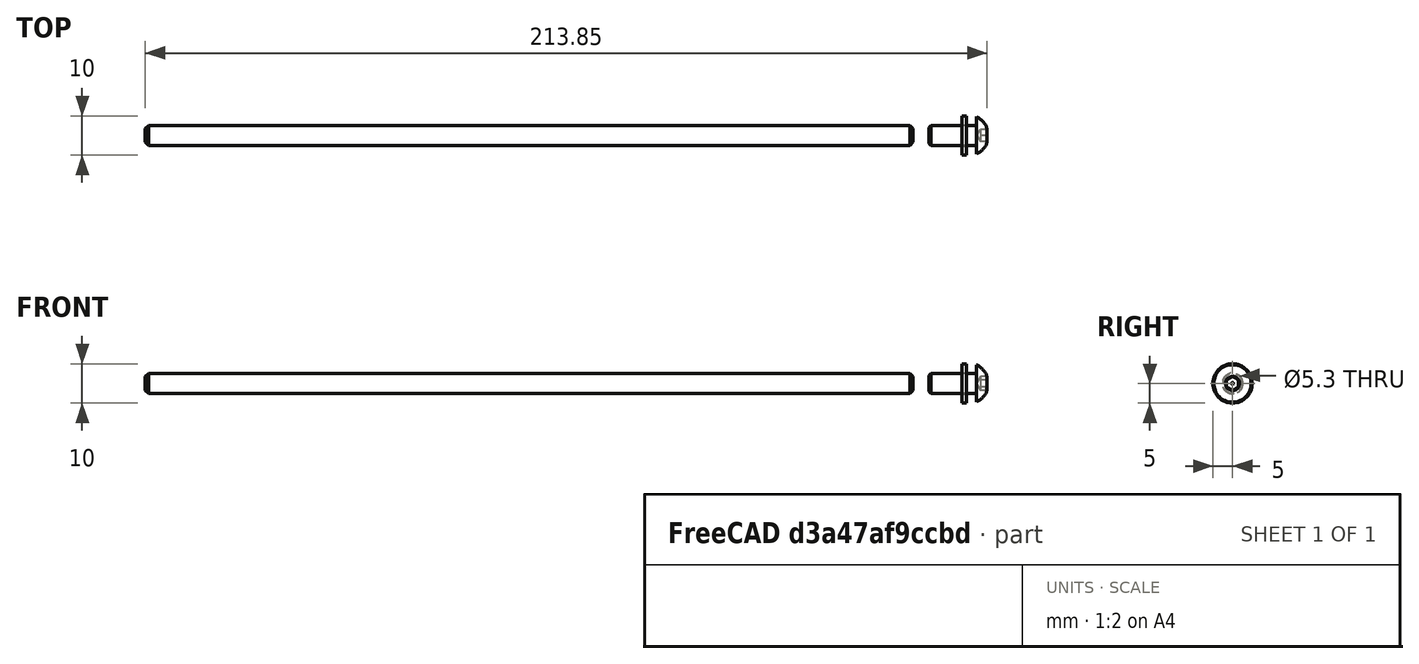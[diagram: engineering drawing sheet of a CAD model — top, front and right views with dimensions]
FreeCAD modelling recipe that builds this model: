
FCSTD DOCUMENT  (FreeCAD 0.21R38887 (Git))
Label: РоликY
License: All rights reserved
LicenseURL: http://en.wikipedia.org/wiki/All_rights_reserved
objects: App::FeaturePython×31, Part::FeaturePython×22, App::Link×7
note: 21 computed .brp shape members not serialized (recipe doc carries the construction recipe); baked Part::Feature solids carry a one-line shape summary decoded from their .brp
EXTERNAL_REF file=ТаблицаПараметров.FCStd obj=Spreadsheet002
EXTERNAL_REF file=роликЗащитыY.FCStd obj=Body
EXTERNAL_REF file=подшипник.FCStd obj=Body
EXTERNAL_REF file=Крепеж.FCStd obj=Body003
EXTERNAL_REF file=ТаблицаПараметров.FCStd obj=Spreadsheet004

FEATURE [Part::FeaturePython] Washer  label="M5-Washer"  # Fasteners workbench fastener (typed FeaturePython)
  InvalidShape = false
  Placement = pos=(110.2,-4e-16,2.59e-14) rot=(-0.707107,0,-0.707107;3.14159rad)
  TreeRank = 2
  ValidateShape = false
  diameter = 6
  invert = false
  matchOuter = false
  offset = 0
  type = 3
  expr: diameter = <<ТаблицаПараметров>>#<<Ролик>>.ShaibaIndex
FEATURE [App::Link] Link003  label="ШайбаПрав"
  AutoLinkLabel = true
  AutoPlacement = true
  LinkPlacement = pos=(-109.5,1e-15,2.55e-14) rot=(0,-1,0;4.71239rad)
  LinkedObject = -> Washer
  Placement = pos=(-109.5,1e-15,2.55e-14) rot=(0,-1,0;4.71239rad)
  SyncGroupVisibility = false
  TreeRank = 4
  _LinkVersion = 1
FEATURE [App::Link] Link006  label="РоликТело"
  AutoLinkLabel = false
  AutoPlacement = true
  LinkPlacement = pos=(1,-4e-16,2.51e-14) rot=(0,0,1;0rad)
  LinkedObject = -> <external роликЗащитыY.FCStd>#Body
  Placement = pos=(1,-4e-16,2.51e-14) rot=(0,0,1;0rad)
  SyncGroupVisibility = false
  TreeRank = 35
  _LinkOwner = 3305
  _LinkVersion = 1
FEATURE [App::Link] Link  label="Подшипник"
  AutoLinkLabel = false
  AutoPlacement = true
  LinkPlacement = pos=(108.7,-4e-16,2.54e-14) rot=(1,0,0;4.71239rad)
  LinkedObject = -> <external подшипник.FCStd>#Body
  Placement = pos=(108.7,-4e-16,2.54e-14) rot=(1,0,0;4.71239rad)
  SyncGroupVisibility = false
  TreeRank = 57
  _LinkOwner = 3305
  _LinkVersion = 1
FEATURE [App::Link] Link007  label="Подшипник2"
  AutoLinkLabel = true
  AutoPlacement = true
  LinkPlacement = pos=(-106.9,2e-16,2.54e-14) rot=(-1,0,0;4.71239rad)
  LinkedObject = -> Link
  Placement = pos=(-106.9,2e-16,2.54e-14) rot=(-1,0,0;4.71239rad)
  SyncGroupVisibility = false
  TreeRank = 58
  _LinkVersion = 1
FEATURE [App::Link] Link008  label="DIN6334_1"
  AutoLinkLabel = true
  AutoPlacement = true
  LinkPlacement = pos=(105.2,0,2.49e-14) rot=(-0.707107,0,0.707107;3.14159rad)
  LinkedObject = -> <external Крепеж.FCStd>#Body003
  Placement = pos=(105.2,0,2.49e-14) rot=(-0.707107,0,0.707107;3.14159rad)
  SyncGroupVisibility = false
  TreeRank = 86
  _LinkVersion = 1
FEATURE [App::Link] Link009  label="DIN6334_2"
  AutoLinkLabel = true
  AutoPlacement = true
  LinkPlacement = pos=(-103.4,-9e-16,2.51e-14) rot=(0,1,0;1.5708rad)
  LinkedObject = -> Link008
  Placement = pos=(-103.4,-9e-16,2.51e-14) rot=(0,1,0;1.5708rad)
  SyncGroupVisibility = false
  TreeRank = 1
  _LinkVersion = 1
FEATURE [Part::FeaturePython] ThreadedRod  label="M5x195.0-ThreadedRod"  # Fasteners workbench fastener (typed FeaturePython)
  InvalidShape = false
  Placement = pos=(-97.3,0,2.71407e-11) rot=(0.707107,0,-0.707107;3.14159rad)
  TreeRank = 97
  ValidateShape = false
  diameter = 7
  diameterCustom = 6
  invert = false
  leftHanded = false
  length = 195
  matchOuter = false
  offset = 0
  pitchCustom = 1
  thread = false
  type = 4
  expr: diameter = <<ТаблицаПараметров>>#<<Ролик>>.ShpilkaIndex
  expr: length = <<ТаблицаПараметров>>#<<Ролик>>.dimL1 - <<ТаблицаПараметров>>#<<Ролик>>.dimH3 * 2 - <<ТаблицаПараметров>>#<<Ролик>>.din6334_Len
FEATURE [Part::FeaturePython] Screw  label="M5x12-Screw"  # Fasteners workbench fastener (typed FeaturePython)
  InvalidShape = false
  Placement = pos=(113.8,-1e-16,1.126e-13) rot=(0,1,0;1.5708rad)
  TreeRank = 106
  ValidateShape = false
  diameter = 3
  invert = false
  leftHanded = false
  length = 2
  lengthCustom = 12
  matchOuter = false
  offset = 0
  thread = false
  type = 40
  expr: diameter = <<ТаблицаПараметров>>#<<Ролик>>.IndexVinta
  expr: length = <<ТаблицаПараметров>>#<<Ролик>>.dlinaVintaInd
FEATURE [App::Link] Link010  label="ВинтПрав"
  AutoLinkLabel = true
  AutoPlacement = true
  LinkPlacement = pos=(-112,1.1e-15,-1.03e-13) rot=(0.707107,0,-0.707107;3.14159rad)
  LinkedObject = -> Screw
  Placement = pos=(-112,1.1e-15,-1.03e-13) rot=(0.707107,0,-0.707107;3.14159rad)
  SyncGroupVisibility = false
  TreeRank = 107
  _LinkVersion = 1
FEATURE [Part::FeaturePython] Parts  # WARN: FeaturePython — macro-defined, semantics opaque (R4)
  Group = -> [Link006,Link,Link007,Link003,Washer,ThreadedRod,Link008,Link009,Screw,Link010]
  GroupMode = 0
  InvalidShape = false
  TreeRank = 0
  ValidateShape = false
  _LinkVersion = 1
FEATURE [Part::FeaturePython] Assembly  label="Ролик"  # WARN: FeaturePython — macro-defined, semantics opaque (R4)
  AutoRelax = true
  BuildShape = 0
  Configuration = 0
  Freeze = false
  Group = -> [Constraints,Elements,Parts]
  InvalidShape = false
  Placement = pos=(0,0,50) rot=(0,0,1;0rad)
  TreeRank = 0
  ValidateShape = false
  Verbose = false
  _LinkVersion = 1
  _SolverType = 1
  _Version = 1
  expr: Configuration.Enum = ТаблицаПараметров#Spreadsheet002.cells[<<B14:|>>]
FEATURE [App::FeaturePython] Constraints  # WARN: FeaturePython — macro-defined, semantics opaque (R4)
  Group = -> [Constraint,Constraint005,Constraint006,Constraint009,Constraint010,Constraint011,Constraint013,Constraint014,Constraint015,Constraint016]
  TreeRank = 0
  _LinkVersion = 1
  _Version = 1
FEATURE [App::FeaturePython] Elements  # WARN: FeaturePython — macro-defined, semantics opaque (R4)
  Group = -> [Element,Element001,Element006,Element007,Element008,Element009,Element010,Element011,Element012,Element013,Element014,Element015,Element016,Element017,Element018,Element019,Element020]
  TreeRank = 0
  _LinkVersion = 1
FEATURE [Part::FeaturePython] Element  label="ТелоПосадкаЛв"  # link proxy (typed FeaturePython)
  Detach = false
  InvalidShape = false
  LinkTransform = true
  LinkedObject = -> Link006 [Revolution.Face5]
  TreeRank = 108
  ValidateShape = false
  _LinkVersion = 1
  _Parent = -> Elements
FEATURE [Part::FeaturePython] Element001  label="ТелоПосадкаПр"  # link proxy (typed FeaturePython)
  Detach = false
  InvalidShape = false
  LinkTransform = true
  LinkedObject = -> Link006 [Revolution.Face7]
  TreeRank = 109
  ValidateShape = false
  _LinkVersion = 1
  _Parent = -> Elements
FEATURE [Part::FeaturePython] Element006  label="ЛвШайбНиз"  # link proxy (typed FeaturePython)
  Detach = false
  InvalidShape = false
  LinkTransform = true
  LinkedObject = -> Washer [Face3]
  TreeRank = 114
  ValidateShape = false
  _LinkVersion = 1
  _Parent = -> Elements
FEATURE [Part::FeaturePython] Element007  label="ПрШайбНиз"  # link proxy (typed FeaturePython)
  Detach = false
  InvalidShape = false
  LinkTransform = true
  LinkedObject = -> Link003 [Face1]
  TreeRank = 115
  ValidateShape = false
  _LinkVersion = 1
  _Parent = -> Elements
FEATURE [Part::FeaturePython] Element008  label="ЛвШайбВерх"  # link proxy (typed FeaturePython)
  Detach = false
  InvalidShape = false
  LinkTransform = true
  LinkedObject = -> Washer [Face1]
  TreeRank = 116
  ValidateShape = false
  _LinkVersion = 1
  _Parent = -> Elements
FEATURE [Part::FeaturePython] Element009  label="ПрШайбВерх"  # link proxy (typed FeaturePython)
  Detach = false
  InvalidShape = false
  LinkTransform = true
  LinkedObject = -> Link003 [Face3]
  TreeRank = 117
  ValidateShape = false
  _LinkVersion = 1
  _Parent = -> Elements
FEATURE [Part::FeaturePython] Element010  label="ЛвГайкаНиз"  # link proxy (typed FeaturePython)
  Detach = false
  InvalidShape = false
  LinkTransform = true
  LinkedObject = -> Link008 [Hole003.Face5]
  TreeRank = 118
  ValidateShape = false
  _LinkVersion = 1
  _Parent = -> Elements
FEATURE [Part::FeaturePython] Element011  label="ПрГайкаНиз"  # link proxy (typed FeaturePython)
  Detach = false
  InvalidShape = false
  LinkTransform = true
  LinkedObject = -> Link009 [Hole003.Face5]
  TreeRank = 119
  ValidateShape = false
  _LinkVersion = 1
  _Parent = -> Elements
FEATURE [Part::FeaturePython] Element012  label="ЛвГайкаВерх"  # link proxy (typed FeaturePython)
  Detach = false
  InvalidShape = false
  LinkTransform = true
  LinkedObject = -> Link008 [Hole003.Face4]
  TreeRank = 120
  ValidateShape = false
  _LinkVersion = 1
  _Parent = -> Elements
FEATURE [Part::FeaturePython] Element013  label="ПрГайкаВерх"  # link proxy (typed FeaturePython)
  Detach = false
  InvalidShape = false
  LinkTransform = true
  LinkedObject = -> Link009 [Hole003.Face4]
  TreeRank = 121
  ValidateShape = false
  _LinkVersion = 1
  _Parent = -> Elements
FEATURE [Part::FeaturePython] Element014  label="ВинтЛв"  # link proxy (typed FeaturePython)
  Detach = false
  InvalidShape = false
  LinkTransform = true
  LinkedObject = -> Screw [Edge4]
  TreeRank = 122
  ValidateShape = false
  _LinkVersion = 1
  _Parent = -> Elements
FEATURE [Part::FeaturePython] Element015  label="ВинтПр"  # link proxy (typed FeaturePython)
  Detach = false
  InvalidShape = false
  LinkTransform = true
  LinkedObject = -> Link010 [Edge4]
  TreeRank = 123
  ValidateShape = false
  _LinkVersion = 1
  _Parent = -> Elements
FEATURE [Part::FeaturePython] Element016  label="ШпилькаСлева"  # link proxy (typed FeaturePython)
  Detach = false
  InvalidShape = false
  LinkTransform = true
  LinkedObject = -> ThreadedRod [Edge6]
  TreeRank = 124
  ValidateShape = false
  _LinkVersion = 1
  _Parent = -> Elements
FEATURE [App::FeaturePython] Constraint  label="Locked"  # WARN: FeaturePython — macro-defined, semantics opaque (R4)
  Disabled = false
  Group = -> [ElementLink]
  TreeRank = 125
  _ConstraintType = 0
  _LinkVersion = 1
  _Parent = -> Constraints
FEATURE [App::FeaturePython] ElementLink  label="ТелоПосадкаЛв"  # link proxy (typed FeaturePython)
  LinkTransform = true
  LinkedObject = -> Element
  TreeRank = 126
  _LinkVersion = 1
  _Parent = -> Constraint
FEATURE [App::FeaturePython] Constraint005  label="Attachment004"  # WARN: FeaturePython — macro-defined, semantics opaque (R4)
  Cascade = false
  Disabled = false
  Group = -> [ElementLink009,ElementLink010]
  Multiply = false
  TreeRank = 139
  _ConstraintType = 45
  _LinkVersion = 1
  _Parent = -> Constraints
FEATURE [App::FeaturePython] ElementLink009  label="ВинтЛв"  # link proxy (typed FeaturePython)
  LinkTransform = true
  LinkedObject = -> Element014
  Offset = pos=(0,0,-1.5) rot=(1,0,0;3.14159rad)
  Placement = pos=(226.1,1.36e-14,-1.004e-13) rot=(0,0,1;3.14159rad)
  TreeRank = 140
  _LinkVersion = 1
  _Parent = -> Constraint005
  expr: Offset.Base.z = -<<ТаблицаПараметров>>#<<ЗащитаТабл>>.toldhinZashita
FEATURE [App::FeaturePython] ElementLink010  label="ЛвШайбВерх"  # link proxy (typed FeaturePython)
  LinkTransform = true
  LinkedObject = -> Element008
  TreeRank = 141
  _LinkVersion = 1
  _Parent = -> Constraint005
FEATURE [App::FeaturePython] Constraint006  label="Attachment005"  # WARN: FeaturePython — macro-defined, semantics opaque (R4)
  Cascade = false
  Disabled = false
  Group = -> [ElementLink011,ElementLink012]
  Multiply = false
  TreeRank = 142
  _ConstraintType = 45
  _LinkVersion = 1
  _Parent = -> Constraints
FEATURE [App::FeaturePython] ElementLink011  label="ВинтПр"  # link proxy (typed FeaturePython)
  LinkTransform = true
  LinkedObject = -> Element015
  Offset = pos=(0,0,-1.5) rot=(1,0,0;3.14159rad)
  Placement = pos=(-222.5,-1.17e-14,-8.8435e-12) rot=(0,0,1;3.14159rad)
  TreeRank = 143
  _LinkVersion = 1
  _Parent = -> Constraint006
  expr: Offset.Base.z = -<<ТаблицаПараметров>>#<<ЗащитаТабл>>.toldhinZashita
FEATURE [App::FeaturePython] ElementLink012  label="ПрШайбВерх"  # link proxy (typed FeaturePython)
  LinkTransform = true
  LinkedObject = -> Element009
  TreeRank = 144
  _LinkVersion = 1
  _Parent = -> Constraint006
FEATURE [App::FeaturePython] Constraint009  label="Attachment008"  # WARN: FeaturePython — macro-defined, semantics opaque (R4)
  Cascade = false
  Disabled = false
  Group = -> [ElementLink018,ElementLink019]
  Multiply = false
  TreeRank = 151
  _ConstraintType = 45
  _LinkVersion = 1
  _Parent = -> Constraints
FEATURE [App::FeaturePython] ElementLink018  label="ЛвГайкаНиз"  # link proxy (typed FeaturePython)
  LinkTransform = true
  LinkedObject = -> Element010
  TreeRank = 153
  _LinkVersion = 1
  _Parent = -> Constraint009
FEATURE [App::FeaturePython] ElementLink019  label="ШпилькаСлева"  # link proxy (typed FeaturePython)
  LinkTransform = true
  LinkedObject = -> Element016
  Offset = pos=(0,0,7.5) rot=(0,0,1;0rad)
  Placement = pos=(-7.5,-4e-16,-2.0692e-12) rot=(0,0,1;0rad)
  TreeRank = 155
  _LinkVersion = 1
  _Parent = -> Constraint009
  expr: Offset.Base.z = <<ТаблицаПараметров>>#<<Ролик>>.din6334_Len / 2
FEATURE [Part::FeaturePython] Element017  label="ЛвПодшНиз"  # link proxy (typed FeaturePython)
  Detach = false
  InvalidShape = false
  LinkTransform = true
  LinkedObject = -> Link [Revolution.Face2]
  TreeRank = 156
  ValidateShape = false
  _LinkVersion = 1
  _Parent = -> Elements
FEATURE [Part::FeaturePython] Element018  label="ПрПодшВерх"  # link proxy (typed FeaturePython)
  Detach = false
  InvalidShape = false
  LinkTransform = true
  LinkedObject = -> Link007 [Revolution.Face2]
  TreeRank = 157
  ValidateShape = false
  _LinkVersion = 1
  _Parent = -> Elements
FEATURE [Part::FeaturePython] Element019  label="ПрПодшНиз"  # link proxy (typed FeaturePython)
  Detach = false
  InvalidShape = false
  LinkTransform = true
  LinkedObject = -> Link007 [Revolution.Face4]
  TreeRank = 158
  ValidateShape = false
  _LinkVersion = 1
  _Parent = -> Elements
FEATURE [Part::FeaturePython] Element020  label="ЛвПодшВерх"  # link proxy (typed FeaturePython)
  Detach = false
  InvalidShape = false
  LinkTransform = true
  LinkedObject = -> Link [Revolution.Face4]
  TreeRank = 159
  ValidateShape = false
  _LinkVersion = 1
  _Parent = -> Elements
FEATURE [App::FeaturePython] Constraint010  label="ТелоЛв"  # WARN: FeaturePython — macro-defined, semantics opaque (R4)
  Cascade = false
  Disabled = false
  Group = -> [ElementLink020,ElementLink021]
  Multiply = false
  TreeRank = 160
  _ConstraintType = 45
  _LinkVersion = 1
  _Parent = -> Constraints
FEATURE [App::FeaturePython] ElementLink020  label="ТелоПосадкаЛв"  # link proxy (typed FeaturePython)
  LinkTransform = true
  LinkedObject = -> Element
  TreeRank = 161
  _LinkVersion = 1
  _Parent = -> Constraint010
FEATURE [App::FeaturePython] ElementLink021  label="ЛвПодшНиз"  # link proxy (typed FeaturePython)
  LinkTransform = true
  LinkedObject = -> Element017
  TreeRank = 162
  _LinkVersion = 1
  _Parent = -> Constraint010
FEATURE [App::FeaturePython] Constraint011  label="ТелоПр"  # WARN: FeaturePython — macro-defined, semantics opaque (R4)
  Cascade = false
  Disabled = false
  Group = -> [ElementLink022,ElementLink023]
  Multiply = false
  TreeRank = 163
  _ConstraintType = 45
  _LinkVersion = 1
  _Parent = -> Constraints
FEATURE [App::FeaturePython] ElementLink022  label="ТелоПосадкаПр"  # link proxy (typed FeaturePython)
  LinkTransform = true
  LinkedObject = -> Element001
  TreeRank = 164
  _LinkVersion = 1
  _Parent = -> Constraint011
FEATURE [App::FeaturePython] ElementLink023  label="ПрПодшНиз"  # link proxy (typed FeaturePython)
  LinkTransform = true
  LinkedObject = -> Element019
  Offset = pos=(0,0,0) rot=(1,0,0;3.14159rad)
  Placement = pos=(-208.8,-1.37e-14,-2.8e-15) rot=(0,0,1;3.14159rad)
  TreeRank = 165
  _LinkVersion = 1
  _Parent = -> Constraint011
FEATURE [App::FeaturePython] Constraint013  label="Attachment011"  # WARN: FeaturePython — macro-defined, semantics opaque (R4)
  Cascade = false
  Disabled = false
  Group = -> [ElementLink026,ElementLink027]
  Multiply = false
  TreeRank = 169
  _ConstraintType = 45
  _LinkVersion = 1
  _Parent = -> Constraints
FEATURE [App::FeaturePython] ElementLink026  label="ПрПодшВерх"  # link proxy (typed FeaturePython)
  LinkTransform = true
  LinkedObject = -> Element018
  TreeRank = 170
  _LinkVersion = 1
  _Parent = -> Constraint013
FEATURE [App::FeaturePython] ElementLink027  label="ПрШайбНиз"  # link proxy (typed FeaturePython)
  LinkTransform = true
  LinkedObject = -> Element007
  TreeRank = 171
  _LinkVersion = 1
  _Parent = -> Constraint013
FEATURE [App::FeaturePython] Constraint014  label="Attachment012"  # WARN: FeaturePython — macro-defined, semantics opaque (R4)
  Cascade = false
  Disabled = false
  Group = -> [ElementLink028,ElementLink029]
  Multiply = false
  TreeRank = 172
  _ConstraintType = 45
  _LinkVersion = 1
  _Parent = -> Constraints
FEATURE [App::FeaturePython] ElementLink028  label="ЛвГайкаВерх"  # link proxy (typed FeaturePython)
  LinkTransform = true
  LinkedObject = -> Element012
  TreeRank = 173
  _LinkVersion = 1
  _Parent = -> Constraint014
FEATURE [App::FeaturePython] ElementLink029  label="ЛвПодшНиз"  # link proxy (typed FeaturePython)
  LinkTransform = true
  LinkedObject = -> Element017
  TreeRank = 174
  _LinkVersion = 1
  _Parent = -> Constraint014
FEATURE [App::FeaturePython] Constraint015  label="Attachment013"  # WARN: FeaturePython — macro-defined, semantics opaque (R4)
  Cascade = false
  Disabled = false
  Group = -> [ElementLink030,ElementLink031]
  Multiply = false
  TreeRank = 175
  _ConstraintType = 45
  _LinkVersion = 1
  _Parent = -> Constraints
FEATURE [App::FeaturePython] ElementLink030  label="ПрГайкаВерх"  # link proxy (typed FeaturePython)
  LinkTransform = true
  LinkedObject = -> Element013
  Placement = pos=(0,1.64e-14,0) rot=(0,0,1;0rad)
  TreeRank = 176
  _LinkVersion = 1
  _Parent = -> Constraint015
FEATURE [App::FeaturePython] ElementLink031  label="ПрПодшНиз"  # link proxy (typed FeaturePython)
  LinkTransform = true
  LinkedObject = -> Element019
  Placement = pos=(0,1.64e-14,0) rot=(0,0,1;0rad)
  TreeRank = 177
  _LinkVersion = 1
  _Parent = -> Constraint015
FEATURE [App::FeaturePython] Constraint016  label="Attachment"  # WARN: FeaturePython — macro-defined, semantics opaque (R4)
  Cascade = false
  Disabled = false
  Group = -> [ElementLink032,ElementLink033]
  Multiply = false
  TreeRank = 178
  _ConstraintType = 45
  _LinkVersion = 1
  _Parent = -> Constraints
FEATURE [App::FeaturePython] ElementLink032  label="ЛвПодшВерх"  # link proxy (typed FeaturePython)
  LinkTransform = true
  LinkedObject = -> Element020
  TreeRank = 179
  _LinkVersion = 1
  _Parent = -> Constraint016
FEATURE [App::FeaturePython] ElementLink033  label="ЛвШайбНиз"  # link proxy (typed FeaturePython)
  LinkTransform = true
  LinkedObject = -> Element006
  TreeRank = 180
  _LinkVersion = 1
  _Parent = -> Constraint016

RESOLVED EXTERNAL PARTS (link-assembly join: the EXTERNAL_REF files above that resolve inside this repo's crawl, each included once):
---- part Крепеж.FCStd = doc fcstd_4da76f0b1cb2 ----
FCSTD DOCUMENT  (FreeCAD 0.20R30972 (Git))
Label: Крепеж
License: All rights reserved
LicenseURL: http://en.wikipedia.org/wiki/All_rights_reserved
objects: Part::FeaturePython×14, App::FeaturePython×9, Sketcher::SketchObject×7, PartDesign::Pad×4, PartDesign::Hole×4, PartDesign::Body×4, App::Link×1
note: 46 computed .brp shape members not serialized (recipe doc carries the construction recipe); baked Part::Feature solids carry a one-line shape summary decoded from their .brp
EXTERNAL_REF file=ТаблицаПараметров.FCStd obj=Spreadsheet002

FEATURE [Sketcher::SketchObject] Sketch004
  FullyConstrained = true
  MapMode = 2
  TreeRank = 11
  sketch-geometry (10):
    g0: LineSegment StartX=-5 StartY=3 StartZ=0 EndX=5 EndY=3 EndZ=0
    g1: LineSegment StartX=5 StartY=3 StartZ=0 EndX=8 EndY=0 EndZ=0
    g2: LineSegment StartX=8 StartY=0 StartZ=0 EndX=8 EndY=-1.2 EndZ=0
    g3: LineSegment StartX=8 StartY=-1.2 StartZ=0 EndX=3.9 EndY=-1.2 EndZ=0
    g4: LineSegment StartX=3.9 StartY=-1.2 StartZ=0 EndX=3.9 EndY=-3 EndZ=0
    g5: LineSegment StartX=3.9 StartY=-3 StartZ=0 EndX=-3.9 EndY=-3 EndZ=0
    g6: LineSegment StartX=-3.9 StartY=-3 StartZ=0 EndX=-3.9 EndY=-1.2 EndZ=0
    g7: LineSegment StartX=-3.9 StartY=-1.2 StartZ=0 EndX=-8 EndY=-1.2 EndZ=0
    g8: LineSegment StartX=-8 StartY=-1.2 StartZ=0 EndX=-8 EndY=0 EndZ=0
    g9: LineSegment StartX=-8 StartY=0 StartZ=0 EndX=-5 EndY=3 EndZ=0
  constraints (28):
    c: PointOnObject(g1,g-1)
    c: Vertical(g2)
    c: Coincident(g3,g2)
    c: Horizontal(g3)
    c: Coincident(g4,g3)
    c: Coincident(g6,g5)
    c: Coincident(g7,g6)
    c: Horizontal(g7)
    c: Coincident(g8,g7)
    c: PointOnObject(g8,g-1)
    c: Vertical(g8)
    c: Coincident(g9,g0)
    c: Coincident(g0,g1)
    c: Coincident(g1,g2)
    c: Coincident(g5,g4)
    c: Vertical(g4)
    c: Vertical(g6)
    c: DistanceX(g0,g0) = 10
    c: Angle(g-1,g9) = 0.785398
    c: Coincident(g9,g8)
    c: Angle(g1,g-1) = 0.785398
    c: Symmetric(g0,g0,g-2)
    c: DistanceX(g5,g5) = 7.8
    c: Symmetric(g5,g4,g-2)
    c: DistanceY(g4,g4) = 1.8
    c: DistanceX(g7,g2) = 16
    c: DistanceY(g6,g6) = 1.8
    c: DistanceY(g5,g0) = 6
FEATURE [PartDesign::Pad] Pad002
  AddSubType = 0
  AlongSketchNormal = false
  CheckUpToFaceLimits = true
  ClaimChildren = false
  Direction = (0,0,1)
  Fit = 0
  FitJoin = 0
  InnerFit = 0
  InnerFitJoin = 0
  InnerTaperAngle = 0
  InnerTaperAngleRev = 0
  Length = 16
  Length2 = 100
  Linearize = true
  NewSolid = false
  Profile = -> Sketch004
  Suppress = false
  TreeRank = 12
  Type = 0
  _ProfileBasedVersion = 1
FEATURE [Sketcher::SketchObject] Sketch005
  FullyConstrained = true
  MapMode = 5
  Placement = pos=(0,-3,0) rot=(1,0,0;1.5708rad)
  Support = -> [Pad002]
  TreeRank = 13
  sketch-geometry (1):
    g0: Circle CenterX=0 CenterY=8 CenterZ=0 NormalX=0 NormalY=0 NormalZ=1 AngleXU=0 Radius=1.6
  constraints (3):
    c: PointOnObject(g0,g-2)
    c: DistanceY(g-1,g0) = 8
    c: Diameter(g0) = 3.2
FEATURE [PartDesign::Hole] Hole002
  AddSubType = 1
  BaseFeature = -> Pad002
  ClaimChildren = false
  CustomThreadClearance = 0
  Depth = 6
  DepthType = 0
  Diameter = 6.6
  DrillForDepth = false
  DrillPoint = 1
  DrillPointAngle = 118
  Fit = 0
  FitJoin = 0
  HoleCutCountersinkAngle = 90
  HoleCutCustomValues = false
  HoleCutDepth = 0
  HoleCutDiameter = 6.1
  HoleCutType = 0
  InnerFit = 0
  InnerFitJoin = 0
  Linearize = true
  ModelThread = true
  NewSolid = false
  Profile = -> Sketch005
  Suppress = false
  Tapered = false
  TaperedAngle = 90
  ThreadClass = 0
  ThreadDepth = 6
  ThreadDepthType = 1
  ThreadDirection = 0
  ThreadFit = 0
  ThreadSize = 14
  ThreadType = 1
  Threaded = false
  TreeRank = 14
  UseCustomThreadClearance = false
  _ProfileBasedVersion = 1
FEATURE [PartDesign::Body] Body002  label="M6T_nut"
  AutoGroupSolids = false
  ClaimAllChildren = false
  ExportMode = 0
  Group = -> [Sketch004,Pad002,Sketch005,Hole002]
  Origin = -> Origin002
  Tip = -> Hole002
  TreeRank = 777
  _ExportChildren = -> [Pad002,Hole002]
  _GroupVersion = 1
FEATURE [App::Link] Link028  label="M6T_nut_1"
  AutoLinkLabel = true
  AutoPlacement = true
  LinkPlacement = pos=(8,-2.7e-15,16.25) rot=(0.57735,-0.57735,-0.57735;2.0944rad)
  LinkedObject = -> Body002
  Placement = pos=(8,-2.7e-15,16.25) rot=(0.57735,-0.57735,-0.57735;2.0944rad)
  SyncGroupVisibility = false
  TreeRank = 692
  _LinkVersion = 1
FEATURE [Part::FeaturePython] Screw002  label="M6x20-Screw"  # Fasteners workbench fastener (typed FeaturePython)
  Placement = pos=(0,0,0) rot=(1,0,0;3.14159rad)
  TreeRank = 200
  diameter = 7
  invert = false
  length = 5
  lengthCustom = 20
  matchOuter = false
  offset = 0
  thread = false
  type = 34
FEATURE [Part::FeaturePython] Parts005  # WARN: FeaturePython — macro-defined, semantics opaque (R4)
  Group = -> [Link028,Screw002]
  GroupMode = 0
  TreeRank = 764
  _LinkVersion = 1
FEATURE [Sketcher::SketchObject] Sketch
  FullyConstrained = true
  MapMode = 2
  TreeRank = 11
  sketch-geometry (10):
    g0: LineSegment StartX=-5 StartY=3 StartZ=0 EndX=5 EndY=3 EndZ=0
    g1: LineSegment StartX=5 StartY=3 StartZ=0 EndX=8 EndY=0 EndZ=0
    g2: LineSegment StartX=8 StartY=0 StartZ=0 EndX=8 EndY=-1.2 EndZ=0
    g3: LineSegment StartX=8 StartY=-1.2 StartZ=0 EndX=3.9 EndY=-1.2 EndZ=0
    g4: LineSegment StartX=3.9 StartY=-1.2 StartZ=0 EndX=3.9 EndY=-3 EndZ=0
    g5: LineSegment StartX=3.9 StartY=-3 StartZ=0 EndX=-3.9 EndY=-3 EndZ=0
    g6: LineSegment StartX=-3.9 StartY=-3 StartZ=0 EndX=-3.9 EndY=-1.2 EndZ=0
    g7: LineSegment StartX=-3.9 StartY=-1.2 StartZ=0 EndX=-8 EndY=-1.2 EndZ=0
    g8: LineSegment StartX=-8 StartY=-1.2 StartZ=0 EndX=-8 EndY=0 EndZ=0
    g9: LineSegment StartX=-8 StartY=0 StartZ=0 EndX=-5 EndY=3 EndZ=0
  constraints (28):
    c: PointOnObject(g1,g-1)
    c: Vertical(g2)
    c: Coincident(g3,g2)
    c: Horizontal(g3)
    c: Coincident(g4,g3)
    c: Coincident(g6,g5)
    c: Coincident(g7,g6)
    c: Horizontal(g7)
    c: Coincident(g8,g7)
    c: PointOnObject(g8,g-1)
    c: Vertical(g8)
    c: Coincident(g9,g0)
    c: Coincident(g0,g1)
    c: Coincident(g1,g2)
    c: Coincident(g5,g4)
    c: Vertical(g4)
    c: Vertical(g6)
    c: DistanceX(g0,g0) = 10
    c: Angle(g-1,g9) = 0.785398
    c: Coincident(g9,g8)
    c: Angle(g1,g-1) = 0.785398
    c: Symmetric(g0,g0,g-2)
    c: DistanceX(g5,g5) = 7.8
    c: Symmetric(g5,g4,g-2)
    c: DistanceY(g4,g4) = 1.8
    c: DistanceX(g7,g2) = 16
    c: DistanceY(g6,g6) = 1.8
    c: DistanceY(g5,g0) = 6
FEATURE [PartDesign::Pad] Pad
  AddSubType = 0
  AlongSketchNormal = false
  CheckUpToFaceLimits = true
  ClaimChildren = false
  Direction = (0,0,1)
  Fit = 0
  FitJoin = 0
  InnerFit = 0
  InnerFitJoin = 0
  InnerTaperAngle = 0
  InnerTaperAngleRev = 0
  Length = 16
  Length2 = 100
  Linearize = true
  NewSolid = false
  Profile = -> Sketch
  Suppress = false
  TreeRank = 12
  Type = 0
  _ProfileBasedVersion = 1
FEATURE [Sketcher::SketchObject] Sketch001
  FullyConstrained = true
  MapMode = 5
  Placement = pos=(0,-3,0) rot=(1,0,0;1.5708rad)
  Support = -> [Pad]
  TreeRank = 13
  sketch-geometry (1):
    g0: Circle CenterX=0 CenterY=8 CenterZ=0 NormalX=0 NormalY=0 NormalZ=1 AngleXU=0 Radius=1.6
  constraints (3):
    c: PointOnObject(g0,g-2)
    c: DistanceY(g-1,g0) = 8
    c: Diameter(g0) = 3.2
FEATURE [PartDesign::Hole] Hole
  AddSubType = 1
  BaseFeature = -> Pad
  ClaimChildren = false
  CustomThreadClearance = 0
  Depth = 6
  DepthType = 0
  Diameter = 3.322
  DrillForDepth = false
  DrillPoint = 1
  DrillPointAngle = 118
  Fit = 0
  FitJoin = 0
  HoleCutCountersinkAngle = 90
  HoleCutCustomValues = false
  HoleCutDepth = 0
  HoleCutDiameter = 6.1
  HoleCutType = 0
  InnerFit = 0
  InnerFitJoin = 0
  Linearize = true
  ModelThread = true
  NewSolid = false
  Profile = -> Sketch001
  Suppress = false
  Tapered = false
  TaperedAngle = 90
  ThreadClass = 0
  ThreadDepth = 6
  ThreadDepthType = 1
  ThreadDirection = 0
  ThreadFit = 0
  ThreadSize = 11
  ThreadType = 1
  Threaded = true
  TreeRank = 14
  UseCustomThreadClearance = false
  _ProfileBasedVersion = 1
FEATURE [PartDesign::Body] Body  label="M4T_nut"
  AutoGroupSolids = false
  ClaimAllChildren = false
  ExportMode = 0
  Group = -> [Sketch,Pad,Sketch001,Hole]
  Origin = -> Origin
  Tip = -> Hole
  TreeRank = 779
  _ExportChildren = -> [Pad,Hole]
  _GroupVersion = 1
FEATURE [Sketcher::SketchObject] Sketch002
  FullyConstrained = true
  MapMode = 2
  TreeRank = 11
  sketch-geometry (10):
    g0: LineSegment StartX=-5 StartY=3 StartZ=0 EndX=5 EndY=3 EndZ=0
    g1: LineSegment StartX=5 StartY=3 StartZ=0 EndX=8 EndY=0 EndZ=0
    g2: LineSegment StartX=8 StartY=0 StartZ=0 EndX=8 EndY=-1.2 EndZ=0
    g3: LineSegment StartX=8 StartY=-1.2 StartZ=0 EndX=3.9 EndY=-1.2 EndZ=0
    g4: LineSegment StartX=3.9 StartY=-1.2 StartZ=0 EndX=3.9 EndY=-3 EndZ=0
    g5: LineSegment StartX=3.9 StartY=-3 StartZ=0 EndX=-3.9 EndY=-3 EndZ=0
    g6: LineSegment StartX=-3.9 StartY=-3 StartZ=0 EndX=-3.9 EndY=-1.2 EndZ=0
    g7: LineSegment StartX=-3.9 StartY=-1.2 StartZ=0 EndX=-8 EndY=-1.2 EndZ=0
    g8: LineSegment StartX=-8 StartY=-1.2 StartZ=0 EndX=-8 EndY=0 EndZ=0
    g9: LineSegment StartX=-8 StartY=0 StartZ=0 EndX=-5 EndY=3 EndZ=0
  constraints (28):
    c: PointOnObject(g1,g-1)
    c: Vertical(g2)
    c: Coincident(g3,g2)
    c: Horizontal(g3)
    c: Coincident(g4,g3)
    c: Coincident(g6,g5)
    c: Coincident(g7,g6)
    c: Horizontal(g7)
    c: Coincident(g8,g7)
    c: PointOnObject(g8,g-1)
    c: Vertical(g8)
    c: Coincident(g9,g0)
    c: Coincident(g0,g1)
    c: Coincident(g1,g2)
    c: Coincident(g5,g4)
    c: Vertical(g4)
    c: Vertical(g6)
    c: DistanceX(g0,g0) = 10
    c: Angle(g-1,g9) = 0.785398
    c: Coincident(g9,g8)
    c: Angle(g1,g-1) = 0.785398
    c: Symmetric(g0,g0,g-2)
    c: DistanceX(g5,g5) = 7.8
    c: Symmetric(g5,g4,g-2)
    c: DistanceY(g4,g4) = 1.8
    c: DistanceX(g7,g2) = 16
    c: DistanceY(g6,g6) = 1.8
    c: DistanceY(g5,g0) = 6
FEATURE [PartDesign::Pad] Pad001
  AddSubType = 0
  AlongSketchNormal = false
  CheckUpToFaceLimits = true
  ClaimChildren = false
  Direction = (0,0,1)
  Fit = 0
  FitJoin = 0
  InnerFit = 0
  InnerFitJoin = 0
  InnerTaperAngle = 0
  InnerTaperAngleRev = 0
  Length = 16
  Length2 = 100
  Linearize = true
  NewSolid = false
  Profile = -> Sketch002
  Suppress = false
  TreeRank = 12
  Type = 0
  _ProfileBasedVersion = 1
FEATURE [Sketcher::SketchObject] Sketch003
  FullyConstrained = true
  MapMode = 5
  Placement = pos=(0,-3,0) rot=(1,0,0;1.5708rad)
  Support = -> [Pad001]
  TreeRank = 13
  sketch-geometry (1):
    g0: Circle CenterX=0 CenterY=8 CenterZ=0 NormalX=0 NormalY=0 NormalZ=1 AngleXU=0 Radius=1.6
  constraints (3):
    c: PointOnObject(g0,g-2)
    c: DistanceY(g-1,g0) = 8
    c: Diameter(g0) = 3.2
FEATURE [PartDesign::Hole] Hole001
  AddSubType = 1
  BaseFeature = -> Pad001
  ClaimChildren = false
  CustomThreadClearance = 0
  Depth = 6
  DepthType = 0
  Diameter = 4.224
  DrillForDepth = false
  DrillPoint = 1
  DrillPointAngle = 118
  Fit = 0
  FitJoin = 0
  HoleCutCountersinkAngle = 90
  HoleCutCustomValues = false
  HoleCutDepth = 0
  HoleCutDiameter = 6.1
  HoleCutType = 0
  InnerFit = 0
  InnerFitJoin = 0
  Linearize = true
  ModelThread = true
  NewSolid = false
  Profile = -> Sketch003
  Suppress = false
  Tapered = false
  TaperedAngle = 90
  ThreadClass = 0
  ThreadDepth = 6
  ThreadDepthType = 1
  ThreadDirection = 0
  ThreadFit = 0
  ThreadSize = 13
  ThreadType = 1
  Threaded = true
  TreeRank = 14
  UseCustomThreadClearance = false
  _ProfileBasedVersion = 1
FEATURE [PartDesign::Body] Body001  label="M5T_nut"
  AutoGroupSolids = false
  ClaimAllChildren = false
  ExportMode = 0
  Group = -> [Sketch002,Pad001,Sketch003,Hole001]
  Origin = -> Origin001
  Tip = -> Hole001
  TreeRank = 780
  _ExportChildren = -> [Pad001,Hole001]
  _GroupVersion = 1
FEATURE [Sketcher::SketchObject] Sketch006
  FullyConstrained = true
  MapMode = 2
  Support = -> [XY_Plane003]
  TreeRank = 11
  expr: Constraints[20] = <<ТаблицаПараметров>>#<<Ролик>>.din6334_D1
  sketch-geometry (8):
    g0: LineSegment StartX=3.75278 StartY=6.5 StartZ=0 EndX=-3.75278 EndY=6.5 EndZ=0
    g1: LineSegment StartX=-3.75278 StartY=6.5 StartZ=0 EndX=-7.50555 EndY=2.04e-14 EndZ=0
    g2: LineSegment StartX=-7.50555 StartY=2.04e-14 StartZ=0 EndX=-3.75278 EndY=-6.5 EndZ=0
    g3: LineSegment StartX=-3.75278 StartY=-6.5 StartZ=0 EndX=3.75278 EndY=-6.5 EndZ=0
    g4: LineSegment StartX=3.75278 StartY=-6.5 StartZ=0 EndX=7.50555 EndY=1.78e-14 EndZ=0
    g5: LineSegment StartX=7.50555 StartY=1.8e-14 StartZ=0 EndX=3.75278 EndY=6.5 EndZ=0
    g6: Circle [constr] CenterX=0 CenterY=0 CenterZ=0 NormalX=0 NormalY=0 NormalZ=1 AngleXU=0 Radius=7.50555
    g7: Circle CenterX=0 CenterY=0 CenterZ=0 NormalX=0 NormalY=0 NormalZ=1 AngleXU=0 Radius=0.5
  constraints (18):
    c: Coincident(g0,g1)
    c: Coincident(g1,g2)
    c: Coincident(g2,g3)
    c: Coincident(g3,g4)
    c: Coincident(g4,g5)
    c: Coincident(g5,g0)
    c: Equal(g0, g1-g5) x5
    c: PointOnObject(g0,g6)
    c: PointOnObject(g1,g6)
    c: PointOnObject(g2,g6)
    c: PointOnObject(g3,g6)
    c: PointOnObject(g4,g6)
    c: PointOnObject(g5,g6)
    c: Horizontal(g0)
    c: Coincident(g6,g7)
    c: Coincident(g6,g-1)
    c: DistanceY(g2,g0) = 13
    c: Diameter(g7) = 1
FEATURE [PartDesign::Pad] Pad003
  AddSubType = 0
  AlongSketchNormal = false
  CheckUpToFaceLimits = true
  ClaimChildren = false
  Direction = (0,0,1)
  Fit = 0
  FitJoin = 0
  InnerFit = 0
  InnerFitJoin = 0
  InnerTaperAngle = 0
  InnerTaperAngleRev = 0
  Length = 24
  Length2 = 100
  Linearize = true
  NewSolid = false
  Profile = -> Sketch006
  Suppress = false
  TreeRank = 12
  Type = 0
  _ProfileBasedVersion = 1
  expr: Length = <<ТаблицаПараметров>>#<<Ролик>>.din6334_Len
FEATURE [PartDesign::Hole] Hole003
  AddSubType = 1
  BaseFeature = -> Pad003
  ClaimChildren = false
  CustomThreadClearance = 0
  Depth = 25
  DepthType = 0
  Diameter = 6.828
  DrillForDepth = false
  DrillPoint = 1
  DrillPointAngle = 118
  Fit = 0
  FitJoin = 0
  HoleCutCountersinkAngle = 90
  HoleCutCustomValues = false
  HoleCutDepth = 0
  HoleCutDiameter = 6.93
  HoleCutType = 0
  InnerFit = 0
  InnerFitJoin = 0
  Linearize = true
  ModelThread = true
  NewSolid = false
  Profile = -> Pad003 [Edge21]
  Suppress = false
  Tapered = false
  TaperedAngle = 90
  ThreadClass = 0
  ThreadDepth = 25
  ThreadDepthType = 0
  ThreadDirection = 0
  ThreadFit = 0
  ThreadSize = 16
  ThreadType = 1
  Threaded = true
  TreeRank = 13
  UseCustomThreadClearance = false
  _ProfileBasedVersion = 1
  expr: ThreadSize = <<ТаблицаПараметров>>#<<Ролик>>.din6334_Index
FEATURE [PartDesign::Body] Body003  label="DIN6334"
  AutoGroupSolids = false
  ClaimAllChildren = false
  ExportMode = 0
  Group = -> [Sketch006,Pad003,Hole003]
  Origin = -> Origin003
  Tip = -> Hole003
  TreeRank = 781
  _ExportChildren = -> [Pad003,Hole003]
  _GroupVersion = 1
FEATURE [Part::FeaturePython] Screw  label="M4x16-Screw"  # Fasteners workbench fastener (typed FeaturePython)
  TreeRank = 782
  diameter = 5
  invert = false
  length = 5
  lengthCustom = 16
  matchOuter = false
  offset = 0
  thread = false
  type = 34
FEATURE [Part::FeaturePython] Screw003  label="M5x12-Screw"  # Fasteners workbench fastener (typed FeaturePython)
  TreeRank = 783
  diameter = 6
  invert = false
  length = 2
  lengthCustom = 12
  matchOuter = false
  offset = 0
  thread = false
  type = 34
FEATURE [App::FeaturePython] Constraints  # WARN: FeaturePython — macro-defined, semantics opaque (R4)
  TreeRank = 785
  _LinkVersion = 1
  _Version = 1
FEATURE [Part::FeaturePython] Parts  # WARN: FeaturePython — macro-defined, semantics opaque (R4)
  Group = -> [Screw003]
  GroupMode = 0
  TreeRank = 787
  _LinkVersion = 1
FEATURE [App::FeaturePython] Constraints006  # WARN: FeaturePython — macro-defined, semantics opaque (R4)
  TreeRank = 791
  _LinkVersion = 1
  _Version = 1
FEATURE [Part::FeaturePython] Parts006  # WARN: FeaturePython — macro-defined, semantics opaque (R4)
  Group = -> [Screw]
  GroupMode = 0
  TreeRank = 793
  _LinkVersion = 1
FEATURE [Part::FeaturePython] Assembly005  label="КрепежМ6Тгайка"  # WARN: FeaturePython — macro-defined, semantics opaque (R4)
  AutoRelax = true
  BuildShape = 0
  Freeze = false
  Group = -> [Constraints005,Elements005,Parts005]
  TreeRank = 778
  Verbose = false
  _LinkVersion = 1
  _SolverType = 1
  _Version = 1
FEATURE [App::FeaturePython] Constraint065  label="Attachment029"  # WARN: FeaturePython — macro-defined, semantics opaque (R4)
  Cascade = false
  Disabled = false
  Group = -> [ElementLink138,ElementLink139]
  Multiply = false
  TreeRank = 773
  _ConstraintType = 45
  _LinkVersion = 1
  _Parent = -> Constraints005
FEATURE [App::FeaturePython] Constraints005  # WARN: FeaturePython — macro-defined, semantics opaque (R4)
  Group = -> [Constraint065]
  TreeRank = 762
  _LinkVersion = 1
  _Version = 1
FEATURE [Part::FeaturePython] Element140  label="Винт"  # link proxy (typed FeaturePython)
  Detach = false
  LinkTransform = true
  LinkedObject = -> Screw002 [Face5]
  TreeRank = 765
  _LinkVersion = 1
  _Parent = -> Elements005
FEATURE [Part::FeaturePython] Element141  label="резьбагайки"  # link proxy (typed FeaturePython)
  Detach = false
  LinkTransform = true
  LinkedObject = -> Link028 [Hole002.Face6]
  TreeRank = 766
  _LinkVersion = 1
  _Parent = -> Elements005
FEATURE [Part::FeaturePython] Element142  label="резьбавинта"  # link proxy (typed FeaturePython)
  Detach = false
  LinkTransform = true
  LinkedObject = -> Screw002 [Face7]
  TreeRank = 767
  _LinkVersion = 1
  _Parent = -> Elements005
FEATURE [App::FeaturePython] ElementLink138  label="резьбавинта"  # link proxy (typed FeaturePython)
  LinkTransform = true
  LinkedObject = -> Element142
  TreeRank = 774
  _LinkVersion = 1
  _Parent = -> Constraint065
FEATURE [App::FeaturePython] ElementLink139  label="резьбагайки"  # link proxy (typed FeaturePython)
  LinkTransform = true
  LinkedObject = -> Element141
  Offset = pos=(0,0,13) rot=(0,0,1;1.5708rad)
  Placement = pos=(-4.4e-15,1.13e-14,-13) rot=(0,0,-1;1.5708rad)
  TreeRank = 775
  _LinkVersion = 1
  _Parent = -> Constraint065
FEATURE [App::FeaturePython] Elements005  # WARN: FeaturePython — macro-defined, semantics opaque (R4)
  Group = -> [Element140,Element141,Element142]
  TreeRank = 763
  _LinkVersion = 1
FEATURE [Part::FeaturePython] Assembly  label="М5х12"  # WARN: FeaturePython — macro-defined, semantics opaque (R4)
  AutoRelax = true
  BuildShape = 0
  Freeze = false
  Group = -> [Constraints,Elements,Parts]
  TreeRank = 784
  Verbose = false
  _LinkVersion = 1
  _SolverType = 1
  _Version = 1
FEATURE [App::FeaturePython] Elements  # WARN: FeaturePython — macro-defined, semantics opaque (R4)
  Group = -> [Element]
  TreeRank = 786
  _LinkVersion = 1
FEATURE [Part::FeaturePython] Element  label="М5_12_посадка"  # link proxy (typed FeaturePython)
  Detach = false
  LinkTransform = true
  LinkedObject = -> Screw003 [Face5]
  TreeRank = 788
  _LinkVersion = 1
  _Parent = -> Elements
FEATURE [Part::FeaturePython] Assembly006  label="М4х16"  # WARN: FeaturePython — macro-defined, semantics opaque (R4)
  AutoRelax = true
  BuildShape = 0
  Freeze = false
  Group = -> [Constraints006,Elements006,Parts006]
  TreeRank = 790
  Verbose = false
  _LinkVersion = 1
  _SolverType = 1
  _Version = 1
FEATURE [App::FeaturePython] Elements006  # WARN: FeaturePython — macro-defined, semantics opaque (R4)
  Group = -> [Element143]
  TreeRank = 792
  _LinkVersion = 1
FEATURE [Part::FeaturePython] Element143  label="М4_16_посадка"  # link proxy (typed FeaturePython)
  Detach = false
  LinkTransform = true
  LinkedObject = -> Screw [Face5]
  TreeRank = 794
  _LinkVersion = 1
  _Parent = -> Elements006
---- part ТаблицаПараметров.FCStd = doc fcstd_60ae2dd5e8f4 ----
FCSTD DOCUMENT  (FreeCAD 0.21R38887 (Git))
Label: ТаблицаПараметров
License: All rights reserved
LicenseURL: http://en.wikipedia.org/wiki/All_rights_reserved
objects: Spreadsheet::Sheet×9
EXTERNAL_REF file=ЧастиСтанка/Станина/Деталі/NEMA23.FCStd obj=Assembly

FEATURE [Spreadsheet::Sheet] Spreadsheet  label="Профиль"
  PythonMode = false
  ShowCells = 0
  TreeRank = 1
  cells = A2=ДлинаПрофиля; B2(Dlina)==<<ТаблСтанина>>.ShirinaStaninu; A3=ШагОтверстийСоединения; B3(ShagOtv)=100; A4=ДиаметрОтверстия; B4(DiametrOtvSoed)=4; A6=Перша висота Т пазу; B6(HTpaz1)=20; A7=Друга висота Т пазу; B7(HTpaz2)=60; A8=КоличествоОтвСоединения; B8(HoleNumberSoed)==trunc(Dlina / ShagOtv) - 1; A9=ДлинаМасиваСоед; B9(DlinaMasivaSoed)==ShagOtv * HoleNumberSoed; A10=ОтступОтКрая; B10(OtstupRels)==(Dlina - DlinaMasivaSoed) / 2
FEATURE [Spreadsheet::Sheet] Spreadsheet001  label="ТаблСтанина"
  PythonMode = false
  ShowCells = 0
  TreeRank = 0
  cells = A2=Ширина; B2(ShirinaStaninu)=480; A3=Количество палок профиля; B3(NumberProfileBody)=10; A4=Высота; B4(RazmerProfilja)=80; A5=Глубина; B5(GlubinaStaninu)==RazmerProfilja * NumberProfileBody
FEATURE [Spreadsheet::Sheet] Spreadsheet002  label="Ролик"
  PythonMode = false
  ShowCells = 0
  TreeRank = 1
  cells = A7=Высота под подшипник; B7(dimH3)==dimH1 + dimH2; C7=висота   подш + висота шайби; A8=Длина общая (без шайб); B8(dimL1)=222; C8=Final lenght; A9=ball radius; B9(ball_radius)==(<<Ролик>>.dimD2 / 2 - <<Ролик>>.diamPodsh / 2) / 3; C9=alpha; D9(alpa)==atan(.ball_radius / .ball_pos_radius); A10=R for ball; B10(ball_pos_radius)==(<<Ролик>>.dimD2 / 2 - <<Ролик>>.diamPodsh / 2) / 2 + <<Ролик>>.diamPodsh / 2; C10=number of ball; D10(ball_number)==trunc(360 / (2 * .alpa)); C11=Длинная гайка; G11=Винт; I11=Подшипник; L11=Труба; N11=Шайба; O11=Шпилька; B12=Inner thread; C12=External dim; D12=Thread index; E12=Lenght; F12=ШайбаИндекс; G12=Индекс винта; H12=Длина винта(index); I12=Диам подш; J12=диад внутр подш; K12=Высота подш.; L12=Диам внешн.; M12=Диам внутр.; N12=Высота шайбы; O12=Индекс; A13=DIN6334 table; B13==dbind(РоликY#Assembly.Configuration.All); C13(din6334_D1)==.C14; D13(din6334_Index)==.D14; E13(din6334_Len)==.E14; F13(ShaibaIndex)==.F14; G13(IndexVinta)==.G14; H13(dlinaVintaInd)==.H14; I13(dimD2)==.I14; J13(diamPodsh)==.J14; K13(dimH1)==.K14; L13(dimD1)==.L14; M13(dimD3)==.M14; N13(dimH2)==.N14; O13(ShpilkaIndex)==.O14; B14=M5v1; C14=8; D14=13; E14=15; F14=6; G14=3; H14=2; I14=14; J14=5; K14=5; L14=16; M14=12; N14=1; O14=7; B15=M5v2; C15=8; D15=13; E15=15; F15=6; G15=3; H15=2; I15=16; J15=5; K15=5; L15=18; M15=14; N15=1; O15=7; B16=M6; C16=10; D16=14; E16=18; F16=7; G16=4; H16=2; I16=19; J16=6; K16=6; L16=21.3; M16=16.1; N16=1.6; O16=8; B17=M8; C17=13; D17=16; E17=24; F17=8; G17=5; H17=3; I17=22; J17=8; K17=7; L17=25; M17=19; N17=1.6; O17=9
  expr: cells.Bind.C13.ZZ13 = tuple(.cells, <<C>> + str(hiddenref(РоликY#Assembly.Configuration) + 14), <<ZZ>> + str(hiddenref(РоликY#Assembly.Configuration) + 14))
FEATURE [Spreadsheet::Sheet] Spreadsheet004  label="ЗащитаТабл"
  PythonMode = false
  ShowCells = 0
  TreeRank = 1
  cells = A2=Ширина 1; B2(dimL1)=45; C2=Слева от П прорези (зависит от опоры и толщины пластины крепления опоры); D2=dimL1; E2=задать формулу; A3=Ширина 2; B3(dimL2)==<<ТаблСтанина>>.GlubinaStaninu; C3=П прорезь Зависит от ширины профиля и количества палок + небольшой зазор (0.2мм); D3=dimL2; A4=Ширина 3; B4(dimL3)==ceil((<<NEMA23Table>>.TotalLen + dimR1 * 2 + 5) / 5) * 5 + 10; C4=Справа от П прорези (motor); D4=dimL3; A5=Высота 1; B5(dimH1)==<<ПластиныY>>.Heigh1; C5=Общая высота защиты; D5=dimH1; E5=висота пластин и защити однакові; A6=Высота 2; B6(dimh2)=80; C6=Высота профиля ; D6=dimh2; A7=Радиус 1; B7(dimR1)==<<Ролик>>.dimD1 / 2; C7=Радиус скругления по углам с роликами; D7=dimR1; A8=Радиус 2; B8(dimR2)=2.5; C8=Крепление роликов; D8=dimR2; A9=Радиус 3; B9(dimR3)==<<ПроставкаYТабл>>.DiamOtvZashitu / 2; C9=Крепление защиты(радиус отверстя); D9=dimR3; A10=Радиус 4; B10(dimR4)=3; C10=Скругление в точках прилегания к профилю; D10=dimR4; A11=Высота 3; B11(dimH3)==<<ПроставкаYТабл>>.Tolshina / 2; C11=Высота винтов крепления защиты; D11=dimH3; A12=ЧислоВинтов1; B12(num1)==<<ПроставкаYТабл>>.NumberHoleZashita; C12=Количество винтов крепления защиты; D12=num1; A13=Шаг1; B13(dimL4)==<<ПроставкаYТабл>>.ShagOtvZash; C13=Расстояние между винтами защиты; D13=dimL4; A14=ДлинаМасива1; B14(dimL5)==num1 * dimL4; C14=Растояние между крайними віинтами защиты; D14=dimL5; A15=Отступ1; B15(dimL6)==(dimL2 - dimL5) / 2; C15=Отступ от начала П прорези до первого винта крепления защиты; D15=dimL6; A16=Толщина листа; B16(toldhinZashita)=1.5; D16=toldhinZashita
FEATURE [Spreadsheet::Sheet] Spreadsheet006  label="ШВП"
  PythonMode = false
  ShowCells = 0
  TreeRank = 2
  cells = A1=ШВП Х; A7=ШВП Y; B7=Длина общая; C7=Диаметр под гайку; D7=Длина резьбы под гайку; E7=Длина вала под крепление; F7=Длина вала под муфту; G7=Диаметр вала под муфту; H7=Шаг ШВП; I7=Диаметр ШВП; B8(lenY)=407; C8(diamYval)=12; D8(lenRezbaYval1)=10; E8(lenValY1)=36; F8(lenMuftaY)=10; G8(diamMuftaY)=10; H8(ShagScrewY)=5; I8(diamSrewY)=16; A12=ШВП Z
FEATURE [Spreadsheet::Sheet] Spreadsheet007  label="ПластиныY"
  PythonMode = false
  ShowCells = 0
  TreeRank = 3
  cells = A1=Параметры пластин для крепления мотора; A3=Ширина пластины; B3(Len1)=145; A4=Висота пластини; B4(Heigh1)=129; A5=ШВП висота ; B5(Heigh2)=100
FEATURE [Spreadsheet::Sheet] Spreadsheet005  label="ПроставкаYТабл"
  Body = -1
  Configuration = 3
  PythonMode = false
  ShowCells = 0
  TreeRank = 5
  cells = A1=Наименование; B1=Значение; C1=Описание параметра; D1=Наименование; E1=Значение; F1=Описание; A2=ДлинаОбщая; D2=Количество точек крепления защиты; E2(NumberHoleZashita)=7; A3=Толщина Проставки; B3(Tolshina)=25; D3=Шаг отверстий под защиту; E3(ShagOtvZash)==<<ТаблСтанина>>.GlubinaStaninu / (NumberHoleZashita + 1); A4=Ширина Проставки; B4(Shirina)=35; D4=ДлинаМасиваКрепежаЗащиты; E4(DlinaMasivaZashita)==NumberHoleZashita * ShagOtvZash; A5=Отступ от края(основание); B5(BodyFirstHole)=20; C5=Отступ от центра; D5(OtstupCenter)==<<ТаблСтанина>>.GlubinaStaninu / 2 - BodyFirstHole; A6=ШагОтверстий; B6(ShagOtverastij)=40; A8=КоличествоОтверстий; B8(HoleNumber)==trunc((<<ТаблСтанина>>.GlubinaStaninu - BodyFirstHole) / ShagOtverastij); A9=ДлинаЛинМасива; B9(DlinaMasiva)==ShagOtverastij * HoleNumber; A11=КоличествоОтвРельс; B11(HoleNumberRels)==trunc(<<ТаблСтанина>>.GlubinaStaninu / ShagRelsa) - 1; A12=ДлинаМасиваРельс; B12(DlinaMasivaRels)==ShagRelsa * HoleNumberRels; A13=ОтступОтКраяРельса; B13(OtstupRels)==(<<ТаблСтанина>>.GlubinaStaninu - DlinaMasivaRels) / 2; A15=КрепежПроставки; B15=ДиаметрОтверстияПодВинт; C15=ДиаметрОтверстия подГоловку; D15=ГлубинаОтверстияПодГоловку; B16(Body_holeDiam)==.B18; C16(BodyHoleDiam)==.C18; D16(BodyHoleGlubina)==.D18; A17=M3; B17=3.2; C17=6; D17=3.4; A18=M4; B18=4.3; C18=8; D18=4.6; A19=M5; B19=5.3; C19=10; D19=5.7; A20=M6; B20=6.4; C20=11; D20=6.8; B24=Ширина Рельсы; C24=Глубина Посадки; D24=Шаг отверстий; E24=Крепление рельсы (индекс резьбы); F24=Длина Винта Крепления; G24=ГлубинаОтверстияПодВИнт; B25(ShirinaPaza)==.B28; C25(GlubunaPaza)==.C28; D25(ShagRelsa)==.D28; E25(indexKreplRels)==.E28; F25(DlinaVintaRels)==.F28; G25(GlubinaOtvRels)==.G28; A26=HGH15; B26=15; C26=4.3; D26=60; E26=11; F26=16; G26=6; A27=HGH20; B27=20; C27=4.6; D27=60; E27=13; F27=16; G27=8; A28=HGH25; B28=23; C28=5.5; D28=60; E28=14; F28=20; G28=8; A32=Крепление боковой защиты; C32=Глубина отверстия под резьбу; D32=Диаметр отверстия в пластине защиты; B33(indexZashita)==.B38; C33(GlubinaOtvZashitu)==.C38; D33(DiamOtvZashitu)==.D38; A34=M3x10; B34=9; C34=10; D34=3.2; A35=M3x12; B35=9; C35=12; D35=3.2; A36=M4x10; B36=11; C36=10; D36=4.3; A37=M4x12; B37=11; C37=12; D37=4.3; A38=M5x10; B38=13; C38=10; D38=5.3; A39=M5x12; B39=13; C39=12; D39=5.3
  expr: Body.Enum = cells[<<A40:|>>]
  expr: Configuration.Enum = cells[<<A17:|>>]
FEATURE [Spreadsheet::Sheet] Spreadsheet009  label="NEMA23Table"
  PythonMode = false
  ShowCells = 0
  TreeRank = 6
  cells = A1=Тип Мотора; B1=Длина мотора; C1=Длина Тела мотора; D1=Длина Вала; E1=Відстань між отворами кріплення; F1=Діаметр кріплення мотора; G1=Діаметр посадки мотора; H1=Діаметр отвору для різьби; B3(TotalLen)==.B12; C3(BodyLen)==.C12; D3(DlinaVala)==.D12; E3(DistOtv)=47.14; F3(DiamOtv)=5; G3(PosadkaMotor)=38.1; H3(diamRezba)=4.2; A4=23HD2304; B4=45; C4=22; D4=63.4; A5=23HD3005; B5=54; C5=31; D5=72.4; A6=23HD4004; B6=56; C6=33; D6=74.4; A7=23HD5401; B7=65; C7=42; D7=83.4; A8=23HD6001; B8=76; C8=53; D8=94.4; A9=23HD8434; B9=100; C9=77; D9=118.4; A10=23HD2601; B10=45; C10=22; D10=63.4; A11=23HD6603; B11=76; C11=53; D11=94.4; A12=23HD7801; B12=82; C12=59; D12=100.4
  expr: cells.Bind.B3.D3 = tuple(.cells, <<B>> + str(hiddenref(NEMA23#Assembly.Base_MotorType) + 4), <<D>> + str(hiddenref(NEMA23#Assembly.Base_MotorType) + 4))
FEATURE [Spreadsheet::Sheet] Spreadsheet010  label="Стол"
  PythonMode = false
  ShowCells = 0
  TreeRank = 7
  cells = A1=Стіл; A2=Ширина столу; B2(StolShirina)=300; A3=Довжина стола; B3(StolDovjuna)=200; A4=Висота столу; B4(StolVusota)=29; A6=Поглиблення під боковий захист; B6(StolPazZahust)=9; A7=Ширина поглиблення під захист; B7(StolPazShuruna)=232; A9=Площадка під каретки; A10=Довжина; B10(StolKaretkaDovjuna)=180; A11=Ширина; B11(StolKaretkuShurina)=222; A12=Ширина каретки; B12(KaretkaShirina)=36; A13=Глибина паза під каретку; B13(KaretkaPaz)=3; A15=Паз під опору; A16=Ширина; B16(OporaShiruna)=72; A17=Довжина; B17(OporaDovjuna)=29; A18=Глибина пазу під опору; B18(OporaPaz)=3
